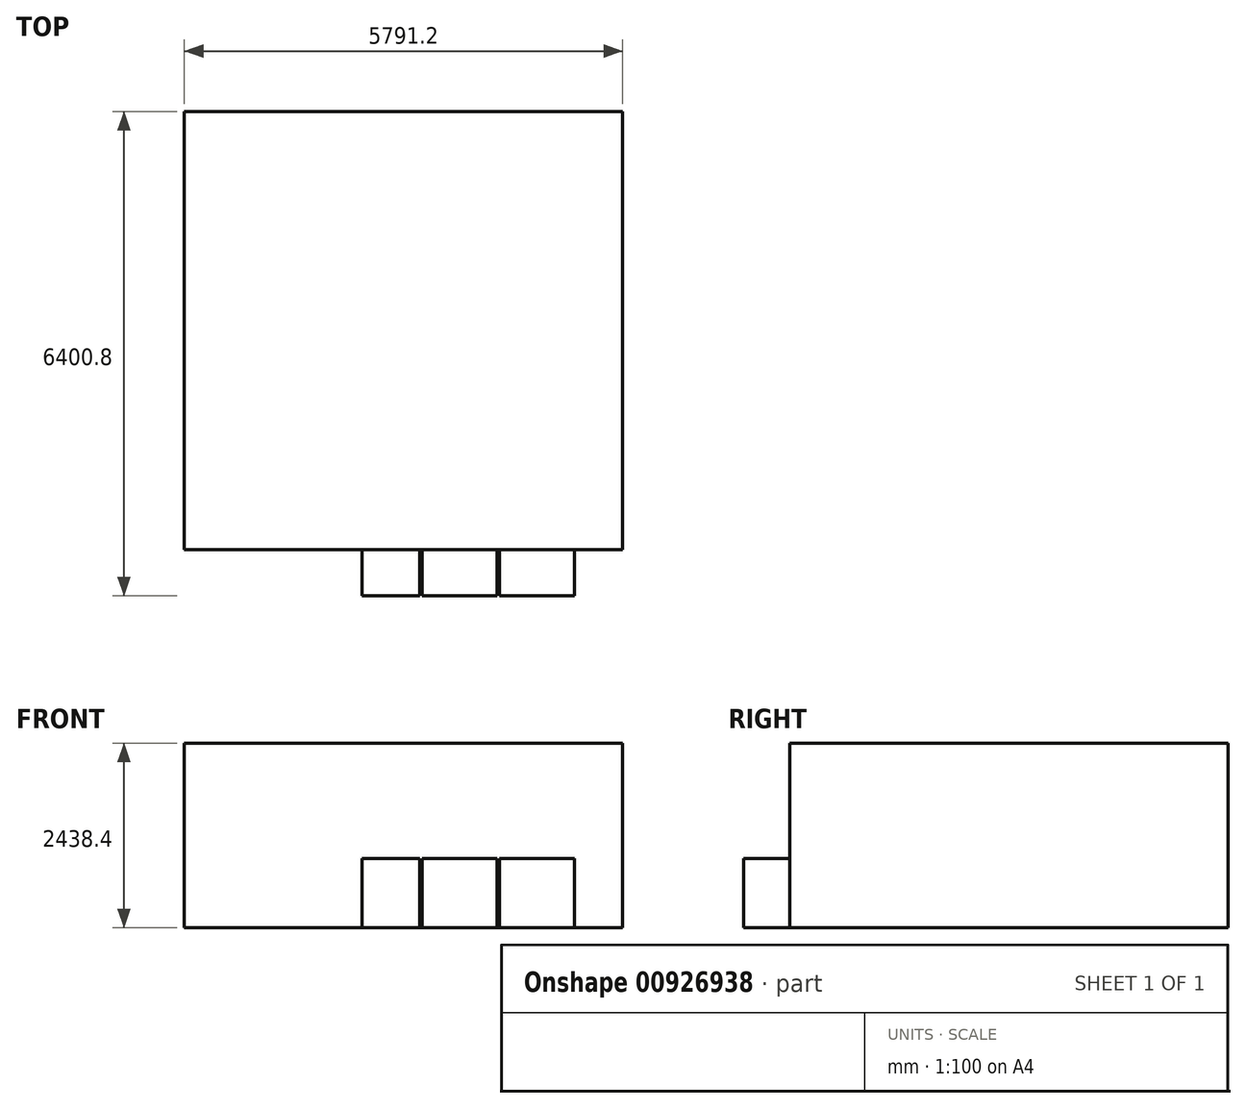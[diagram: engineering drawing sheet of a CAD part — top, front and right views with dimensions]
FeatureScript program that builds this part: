
annotation { "Feature Type Name" : "Feature", "Feature Type Description" : "" }
export const myFeature = defineFeature(function(context is Context, id is Id, definition is map)
    precondition{}
    {
        {
            var Q0;
            Q0=qCreatedBy(makeId("Top.planeOp"),FACE);
            var sketch = newSketch(context, id + "F0", { "sketchPlane" : qUnion([Q0])});
            skLineSegment(sketch, "E0.bottom", {"start": v(2895.6, 2895.6) * mm, "end": v(-2895.6, 2895.6) * mm});
            skLineSegment(sketch, "E0.top", {"start": v(2895.6, -2895.6) * mm, "end": v(-2895.6, -2895.6) * mm});
            skLineSegment(sketch, "E0.left", {"start": v(2895.6, 2895.6) * mm, "end": v(2895.6, -2895.6) * mm});
            skLineSegment(sketch, "E0.right", {"start": v(-2895.6, 2895.6) * mm, "end": v(-2895.6, -2895.6) * mm});
            skPoint(sketch, "E0.middle", {"position": v(0, 0) * mm});
            skSolve(sketch);
        }
        {
            var Q0;
            Q0=qSketchRegion(id+"F0",true);
            extrude(context, id + "F1", {"entities" : qUnion([Q0]), "depth" : 2438.4 * mm, "offsetDistance" : 30.48 * mm});
        }
        {
            var Q0;
            Q0=makeQuery(id+"F1.opExtrude","SWEPT_FACE",FACE,{"disambiguationData":[OSD([sQuery(id+"F0.wireOp",EDGE,"E0.top")])]});
            var sketch = newSketch(context, id + "F2", { "sketchPlane" : qUnion([Q0])});
            skLineSegment(sketch, "E1", {"start": v(2895.6, 0) * mm, "end": v(2286, 0) * mm, "construction": true});
            skLineSegment(sketch, "E2", {"start": v(2286, 0) * mm, "end": v(2255.52, 0) * mm});
            skLineSegment(sketch, "E3", {"start": v(2255.52, 0) * mm, "end": v(1264.92, 0) * mm});
            skLineSegment(sketch, "E4", {"start": v(1264.92, 0) * mm, "end": v(1234.44, 0) * mm});
            skLineSegment(sketch, "E5", {"start": v(1234.44, 0) * mm, "end": v(243.84, 0) * mm});
            skLineSegment(sketch, "E6", {"start": v(243.84, 0) * mm, "end": v(213.36, 0) * mm});
            skLineSegment(sketch, "E7", {"start": v(213.36, 0) * mm, "end": v(-548.64, 0) * mm});
            skLineSegment(sketch, "E8", {"start": v(-548.64, 0) * mm, "end": v(-548.64, 914.4) * mm});
            skLineSegment(sketch, "E9", {"start": v(-548.64, 914.4) * mm, "end": v(213.36, 914.4) * mm});
            skLineSegment(sketch, "E10", {"start": v(213.36, 914.4) * mm, "end": v(213.36, 0) * mm});
            skLineSegment(sketch, "E11", {"start": v(243.84, 0) * mm, "end": v(243.84, 914.4) * mm});
            skLineSegment(sketch, "E12", {"start": v(243.84, 914.4) * mm, "end": v(1234.44, 914.4) * mm});
            skLineSegment(sketch, "E13", {"start": v(1234.44, 914.4) * mm, "end": v(1234.44, 0) * mm});
            skLineSegment(sketch, "E14", {"start": v(1264.92, 0) * mm, "end": v(1264.92, 914.4) * mm});
            skLineSegment(sketch, "E15", {"start": v(1264.92, 914.4) * mm, "end": v(2255.52, 914.4) * mm});
            skLineSegment(sketch, "E16", {"start": v(2255.52, 914.4) * mm, "end": v(2255.52, 0) * mm});
            skSolve(sketch);
        }
        {
            var Q0;
            Q0 = qSketchRegion(id + "F2", true);
            extrude(context, id + "F3", {"entities" : qUnion([Q0]), "operationType" : NewBodyOperationType.ADD, "depth" : 609.6 * mm, "offsetDistance" : 30.48 * mm});
        }
    });
